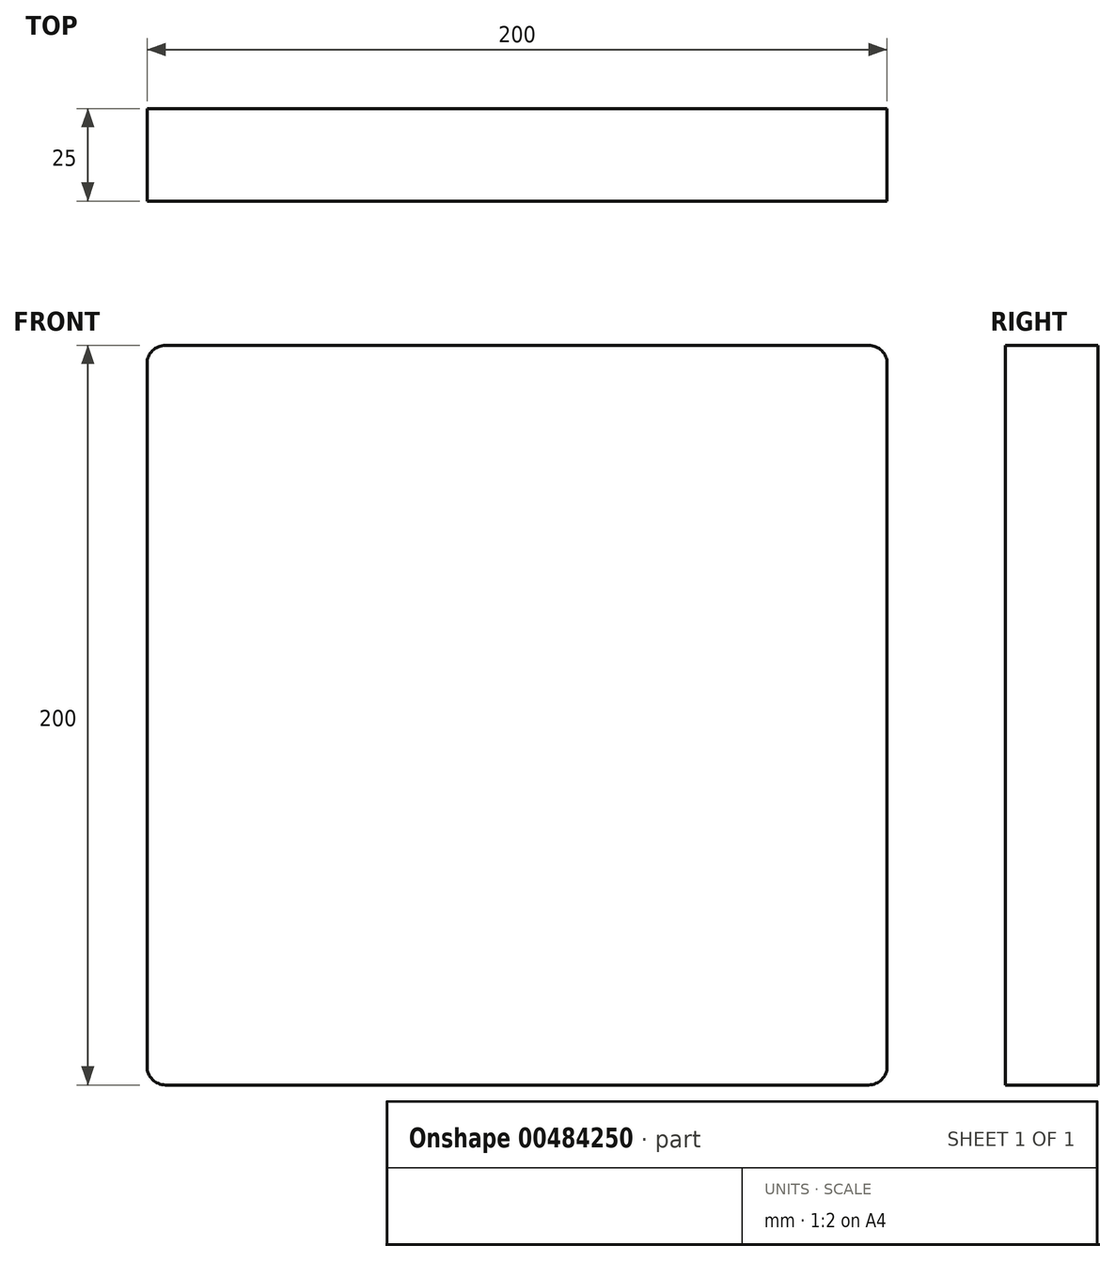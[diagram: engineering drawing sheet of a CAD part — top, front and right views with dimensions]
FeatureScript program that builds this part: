
annotation { "Feature Type Name" : "Feature", "Feature Type Description" : "" }
export const myFeature = defineFeature(function(context is Context, id is Id, definition is map)
    precondition{}
    {
        {
            var Q0;
            Q0=qCreatedBy(makeId("Front.planeOp"),FACE);
            var sketch = newSketch(context, id + "F0", { "sketchPlane" : qUnion([Q0])});
            skLineSegment(sketch, "E0.bottom", {"start": v(-95.35, 124.67) * mm, "end": v(94.65, 124.67) * mm});
            skLineSegment(sketch, "E0.top", {"start": v(-95.35, -75.33) * mm, "end": v(94.65, -75.33) * mm});
            skLineSegment(sketch, "E0.left", {"start": v(-100.35, 119.67) * mm, "end": v(-100.35, -70.33) * mm});
            skLineSegment(sketch, "E0.right", {"start": v(99.65, 119.67) * mm, "end": v(99.65, -70.33) * mm});
            skPoint(sketch, "E1.visualSharp", {"position": v(-100.35, 124.67) * mm});
            skArc(sketch, "E1.filletArc", {"start": v(-95.35, 124.67) * mm, "mid": v(-98.89, 123.2) * mm, "end": v(-100.35, 119.67) * mm});
            skPoint(sketch, "E2.visualSharp", {"position": v(99.65, 124.67) * mm});
            skArc(sketch, "E2.filletArc", {"start": v(99.65, 119.67) * mm, "mid": v(98.18, 123.2) * mm, "end": v(94.65, 124.67) * mm});
            skPoint(sketch, "E3.visualSharp", {"position": v(99.65, -75.33) * mm});
            skArc(sketch, "E3.filletArc", {"start": v(94.65, -75.33) * mm, "mid": v(98.18, -73.86) * mm, "end": v(99.65, -70.33) * mm});
            skPoint(sketch, "E4.visualSharp", {"position": v(-100.35, -75.33) * mm});
            skArc(sketch, "E4.filletArc", {"start": v(-100.35, -70.33) * mm, "mid": v(-98.89, -73.86) * mm, "end": v(-95.35, -75.33) * mm});
            skSolve(sketch);
        }
        {
            var Q0;
            Q0 = qSketchRegion(id + "F0", true);
            extrude(context, id + "F1", {"entities" : qUnion([Q0]), "depth" : 25 * mm});
        }
    });
